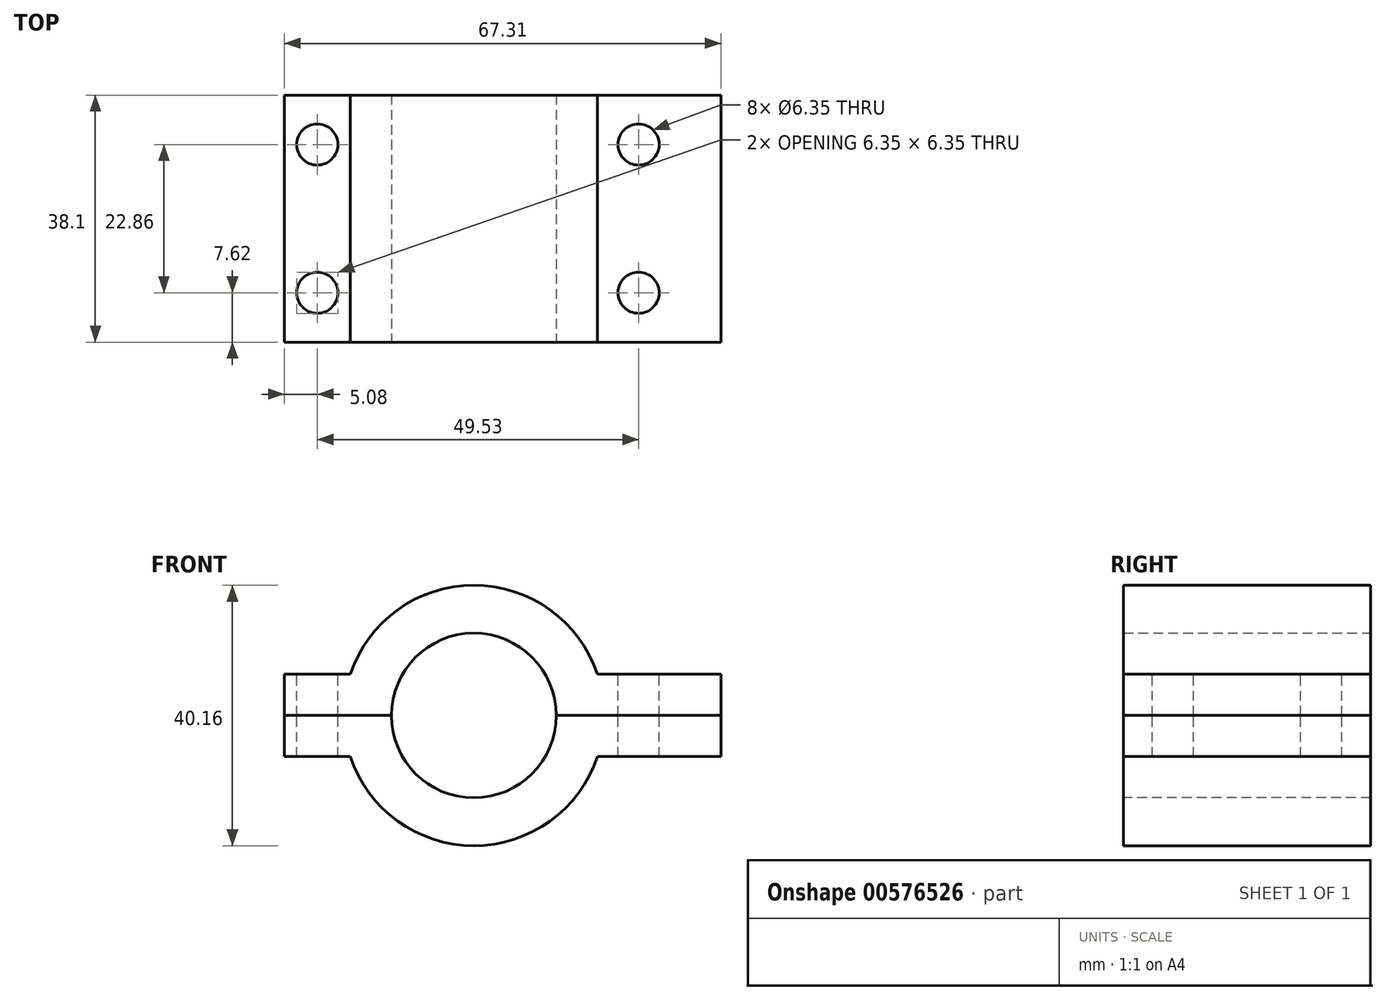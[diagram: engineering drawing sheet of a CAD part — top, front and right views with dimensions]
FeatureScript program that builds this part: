
annotation { "Feature Type Name" : "Feature", "Feature Type Description" : "" }
export const myFeature = defineFeature(function(context is Context, id is Id, definition is map)
    precondition{}
    {
        {
            var Q0;
            Q0=qCreatedBy(makeId("Front.planeOp"),FACE);
            var sketch = newSketch(context, id + "F0", { "sketchPlane" : qUnion([Q0])});
            skLineSegment(sketch, "E0", {"start": v(0, 0) * mm, "end": v(19.05, 0) * mm});
            skLineSegment(sketch, "E1", {"start": v(19.05, 0) * mm, "end": v(19.05, 6.35) * mm});
            skLineSegment(sketch, "E2", {"start": v(19.05, 6.35) * mm, "end": v(0, 6.35) * mm});
            skLineSegment(sketch, "E3", {"start": v(0, 0) * mm, "end": v(-6.35, 0) * mm});
            skArc(sketch, "E4", {"start": v(0, 6.35) * mm, "mid": v(-19.05, 20.08) * mm, "end": v(-38.1, 6.35) * mm});
            skArc(sketch, "E5", {"start": v(-6.35, 0) * mm, "mid": v(-19.05, 12.7) * mm, "end": v(-31.75, 0) * mm});
            skLineSegment(sketch, "E6", {"start": v(-31.75, 0) * mm, "end": v(-48.26, 0) * mm});
            skLineSegment(sketch, "E7", {"start": v(-48.26, 0) * mm, "end": v(-48.26, 6.35) * mm});
            skLineSegment(sketch, "E8", {"start": v(-48.26, 6.35) * mm, "end": v(-38.1, 6.35) * mm});
            skSolve(sketch);
        }
        {
            var Q0;
            Q0=makeQuery(id+"F0.imprint","IMPRINT",FACE,{"disambiguationData":[TD([[makeQuery(id+"F0.imprint","IMPRINT",EDGE,{"derivedFrom":sQuery(id+"F0.wireOp",EDGE,"E0")}),1.0]])]});
            extrude(context, id + "F1", {"entities" : qUnion([Q0]), "depth" : 38.1 * mm, "offsetDistance" : 25.4 * mm});
        }
        {
            var Q0;
            Q0=makeQuery(id+"F1.opExtrude","SWEPT_FACE",FACE,{"disambiguationData":[OSD([sQuery(id+"F0.wireOp",EDGE,"E6")])]});
            var sketch = newSketch(context, id + "F2", { "sketchPlane" : qUnion([Q0])});
            skLineSegment(sketch, "E9", {"start": v(-76.29, 19.05) * mm, "end": v(56.32, 19.05) * mm});
            skSolve(sketch);
        }
        {
            var Q0;
            Q0=makeQuery(id+"F1.opExtrude","SWEPT_BODY",BODY,{"disambiguationData":[OSD([sQuery(id+"F0.wireOp",EDGE,"E0"),sQuery(id+"F0.wireOp",EDGE,"E1"),sQuery(id+"F0.wireOp",EDGE,"E2"),sQuery(id+"F0.wireOp",EDGE,"E3"),sQuery(id+"F0.wireOp",EDGE,"E4"),sQuery(id+"F0.wireOp",EDGE,"E5"),sQuery(id+"F0.wireOp",EDGE,"E6"),sQuery(id+"F0.wireOp",EDGE,"E7"),sQuery(id+"F0.wireOp",EDGE,"E8")])]});
            var Q1;
            Q1=sQuery(id+"F2.wireOp",EDGE,"E9");
            circularPattern(context, id + "F3", {"entities" : qUnion([Q0]), "axis" : qUnion([Q1]), "angle" : 360 * degree, "instanceCount" : 2, "equalSpace" : true});
        }
        {
            var Q0;
            Q0=makeQuery(id+"F1.opExtrude","SWEPT_FACE",FACE,{"disambiguationData":[OSD([sQuery(id+"F0.wireOp",EDGE,"E8")])]});
            var sketch = newSketch(context, id + "F4", { "sketchPlane" : qUnion([Q0])});
            skCircle(sketch, "E10", {"center": v(-43.18, -7.62) * mm, "radius": 3.18 * mm});
            skCircle(sketch, "E11", {"center": v(-43.18, -30.48) * mm, "radius": 3.18 * mm});
            skCircle(sketch, "E12", {"center": v(6.35, -7.62) * mm, "radius": 3.18 * mm});
            skCircle(sketch, "E13", {"center": v(6.35, -30.48) * mm, "radius": 3.18 * mm});
            skSolve(sketch);
        }
        {
            var Q0;
            Q0=makeQuery(id+"F4.imprint","IMPRINT",FACE,{"disambiguationData":[TD([[makeQuery(id+"F4.imprint","IMPRINT",EDGE,{"derivedFrom":sQuery(id+"F4.wireOp",EDGE,"E12")}),1.0]])]});
            var Q1;
            Q1=makeQuery(id+"F4.imprint","IMPRINT",FACE,{"disambiguationData":[TD([[makeQuery(id+"F4.imprint","IMPRINT",EDGE,{"derivedFrom":sQuery(id+"F4.wireOp",EDGE,"E13")}),1.0]])]});
            var Q2;
            Q2=makeQuery(id+"F4.imprint","IMPRINT",FACE,{"disambiguationData":[TD([[makeQuery(id+"F4.imprint","IMPRINT",EDGE,{"derivedFrom":sQuery(id+"F4.wireOp",EDGE,"E11")}),1.0]])]});
            var Q3;
            Q3=makeQuery(id+"F4.imprint","IMPRINT",FACE,{"disambiguationData":[TD([[makeQuery(id+"F4.imprint","IMPRINT",EDGE,{"derivedFrom":sQuery(id+"F4.wireOp",EDGE,"E10")}),1.0]])]});
            extrude(context, id + "F5", {"entities" : qUnion([Q0, Q1, Q2, Q3]), "operationType" : NewBodyOperationType.REMOVE, "oppositeDirection" : true, "depth" : 25.4 * mm, "offsetDistance" : 25.4 * mm});
        }
    });
